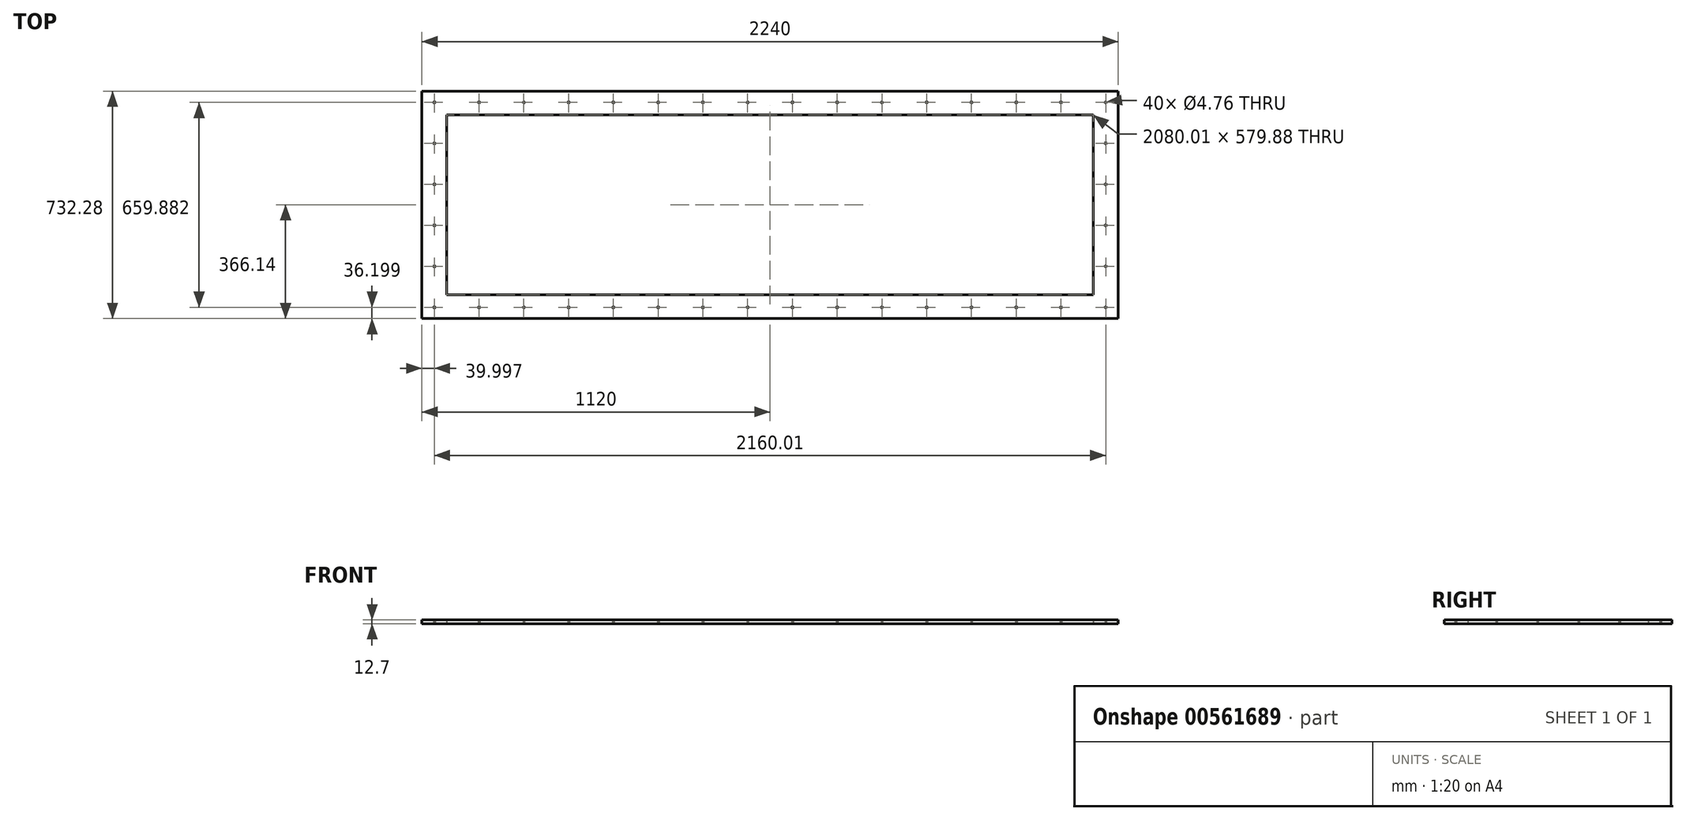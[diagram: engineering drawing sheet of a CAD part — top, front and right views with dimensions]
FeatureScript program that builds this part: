
annotation { "Feature Type Name" : "Feature", "Feature Type Description" : "" }
export const myFeature = defineFeature(function(context is Context, id is Id, definition is map)
    precondition{}
    {
        {
            var Q0;
            Q0=qCreatedBy(makeId("Top.planeOp"),FACE);
            var sketch = newSketch(context, id + "F0", { "sketchPlane" : qUnion([Q0])});
            skLineSegment(sketch, "E0.bottom", {"start": v(1040, 289.94) * mm, "end": v(-1040, 289.94) * mm});
            skLineSegment(sketch, "E0.top", {"start": v(1040, -289.94) * mm, "end": v(-1040, -289.94) * mm});
            skLineSegment(sketch, "E0.left", {"start": v(1040, 289.94) * mm, "end": v(1040, -289.94) * mm});
            skLineSegment(sketch, "E0.right", {"start": v(-1040, 289.94) * mm, "end": v(-1040, -289.94) * mm});
            skPoint(sketch, "E0.middle", {"position": v(0, 0) * mm});
            skLineSegment(sketch, "E1.bottom", {"start": v(1120, 366.14) * mm, "end": v(-1120, 366.14) * mm});
            skLineSegment(sketch, "E1.top", {"start": v(1120, -366.14) * mm, "end": v(-1120, -366.14) * mm});
            skLineSegment(sketch, "E1.left", {"start": v(1120, 366.14) * mm, "end": v(1120, -366.14) * mm});
            skLineSegment(sketch, "E1.right", {"start": v(-1120, 366.14) * mm, "end": v(-1120, -366.14) * mm});
            skLineSegment(sketch, "E2.bottom", {"start": v(1080, 329.94) * mm, "end": v(-1080, 329.94) * mm, "construction": true});
            skLineSegment(sketch, "E2.top", {"start": v(1080, -329.94) * mm, "end": v(-1080, -329.94) * mm, "construction": true});
            skLineSegment(sketch, "E2.left", {"start": v(1080, 329.94) * mm, "end": v(1080, -329.94) * mm, "construction": true});
            skLineSegment(sketch, "E2.right", {"start": v(-1080, 329.94) * mm, "end": v(-1080, -329.94) * mm, "construction": true});
            skPoint(sketch, "E3", {"position": v(-1080, 329.94) * mm});
            skPoint(sketch, "E4", {"position": v(1080, 329.94) * mm});
            skPoint(sketch, "E5", {"position": v(1080, -329.94) * mm});
            skPoint(sketch, "E6", {"position": v(-1080, -329.94) * mm});
            skPoint(sketch, "E7.1.0.0", {"position": v(-936, 329.94) * mm});
            skPoint(sketch, "E7.2.0.0", {"position": v(-792, 329.94) * mm});
            skPoint(sketch, "E7.3.0.0", {"position": v(-648, 329.94) * mm});
            skPoint(sketch, "E7.4.0.0", {"position": v(-504, 329.94) * mm});
            skPoint(sketch, "E7.5.0.0", {"position": v(-360, 329.94) * mm});
            skPoint(sketch, "E7.6.0.0", {"position": v(-216, 329.94) * mm});
            skPoint(sketch, "E7.7.0.0", {"position": v(-72, 329.94) * mm});
            skPoint(sketch, "E7.8.0.0", {"position": v(72, 329.94) * mm});
            skPoint(sketch, "E7.9.0.0", {"position": v(216, 329.94) * mm});
            skPoint(sketch, "E7.10.0.0", {"position": v(360, 329.94) * mm});
            skPoint(sketch, "E7.11.0.0", {"position": v(504, 329.94) * mm});
            skPoint(sketch, "E7.12.0.0", {"position": v(648, 329.94) * mm});
            skPoint(sketch, "E7.13.0.0", {"position": v(792, 329.94) * mm});
            skPoint(sketch, "E7.14.0.0", {"position": v(936, 329.94) * mm});
            skLineSegment(sketch, "E7.direction1", {"start": v(-1080, 329.94) * mm, "end": v(-936, 329.94) * mm, "construction": true});
            skPoint(sketch, "E8.0.1.0", {"position": v(-1080, 197.96) * mm});
            skPoint(sketch, "E8.0.2.0", {"position": v(-1080, 65.98) * mm});
            skPoint(sketch, "E8.0.3.0", {"position": v(-1080, -66) * mm});
            skPoint(sketch, "E8.0.4.0", {"position": v(-1080, -197.97) * mm});
            skPoint(sketch, "E8.0.5.0", {"position": v(-1080, -329.95) * mm});
            skLineSegment(sketch, "E8.direction1", {"start": v(-1080, 329.94) * mm, "end": v(-1054.6, 329.94) * mm, "construction": true});
            skLineSegment(sketch, "E8.direction2", {"start": v(-1080, 329.94) * mm, "end": v(-1080, 197.96) * mm, "construction": true});
            skPoint(sketch, "E9.1.0.0", {"position": v(-936, -329.94) * mm});
            skPoint(sketch, "E9.2.0.0", {"position": v(-792, -329.94) * mm});
            skPoint(sketch, "E9.3.0.0", {"position": v(-648, -329.94) * mm});
            skPoint(sketch, "E9.4.0.0", {"position": v(-504, -329.94) * mm});
            skPoint(sketch, "E9.5.0.0", {"position": v(-360, -329.94) * mm});
            skPoint(sketch, "E9.6.0.0", {"position": v(-216, -329.94) * mm});
            skPoint(sketch, "E9.7.0.0", {"position": v(-72, -329.94) * mm});
            skPoint(sketch, "E9.8.0.0", {"position": v(72, -329.94) * mm});
            skPoint(sketch, "E9.9.0.0", {"position": v(216, -329.94) * mm});
            skPoint(sketch, "E9.10.0.0", {"position": v(360, -329.94) * mm});
            skPoint(sketch, "E9.11.0.0", {"position": v(504, -329.94) * mm});
            skPoint(sketch, "E9.12.0.0", {"position": v(648, -329.94) * mm});
            skPoint(sketch, "E9.13.0.0", {"position": v(792, -329.94) * mm});
            skPoint(sketch, "E9.14.0.0", {"position": v(936, -329.94) * mm});
            skLineSegment(sketch, "E9.direction1", {"start": v(-1080, -329.94) * mm, "end": v(-936, -329.94) * mm, "construction": true});
            skPoint(sketch, "E10.0.1.0", {"position": v(1080, -197.96) * mm});
            skPoint(sketch, "E10.0.2.0", {"position": v(1080, -65.98) * mm});
            skPoint(sketch, "E10.0.3.0", {"position": v(1080, 66) * mm});
            skPoint(sketch, "E10.0.4.0", {"position": v(1080, 197.97) * mm});
            skPoint(sketch, "E10.0.5.0", {"position": v(1080, 329.95) * mm});
            skLineSegment(sketch, "E10.direction1", {"start": v(1080, -329.94) * mm, "end": v(1080, -329.94) * mm});
            skLineSegment(sketch, "E10.direction2", {"start": v(1080, -329.94) * mm, "end": v(1080, -197.96) * mm, "construction": true});
            skSolve(sketch);
        }
        {
            var Q0;
            Q0=makeQuery(id+"F0.imprint","IMPRINT",FACE,{"disambiguationData":[TD([[makeQuery(id+"F0.imprint","IMPRINT",EDGE,{"derivedFrom":sQuery(id+"F0.wireOp",EDGE,"E0.bottom")}),-1.0]])]});
            extrude(context, id + "F1", {"entities" : qUnion([Q0]), "depth" : 12.7 * mm, "offsetDistance" : 25.4 * mm});
        }
        {
            var Q0;
            Q0=sQuery(id+"F0.wireOp",VERTEX,"E7.1.0.0");
            var Q1;
            Q1=sQuery(id+"F0.wireOp",VERTEX,"E7.2.0.0");
            var Q2;
            Q2=sQuery(id+"F0.wireOp",VERTEX,"E7.3.0.0");
            var Q3;
            Q3=sQuery(id+"F0.wireOp",VERTEX,"E7.4.0.0");
            var Q4;
            Q4=sQuery(id+"F0.wireOp",VERTEX,"E7.5.0.0");
            var Q5;
            Q5=sQuery(id+"F0.wireOp",VERTEX,"E2.right.start");
            var Q6;
            Q6=sQuery(id+"F0.wireOp",VERTEX,"E8.0.1.0");
            var Q7;
            Q7=sQuery(id+"F0.wireOp",VERTEX,"E8.0.2.0");
            var Q8;
            Q8=sQuery(id+"F0.wireOp",VERTEX,"E8.0.4.0");
            var Q9;
            Q9=sQuery(id+"F0.wireOp",VERTEX,"E2.right.end");
            var Q10;
            Q10=sQuery(id+"F0.wireOp",VERTEX,"E9.1.0.0");
            var Q11;
            Q11=sQuery(id+"F0.wireOp",VERTEX,"E9.2.0.0");
            var Q12;
            Q12=sQuery(id+"F0.wireOp",VERTEX,"E8.0.3.0");
            var Q13;
            Q13=sQuery(id+"F0.wireOp",VERTEX,"E9.3.0.0");
            var Q14;
            Q14=sQuery(id+"F0.wireOp",VERTEX,"E9.4.0.0");
            var Q15;
            Q15=sQuery(id+"F0.wireOp",VERTEX,"E9.5.0.0");
            var Q16;
            Q16=sQuery(id+"F0.wireOp",VERTEX,"E9.6.0.0");
            var Q17;
            Q17=sQuery(id+"F0.wireOp",VERTEX,"E9.7.0.0");
            var Q18;
            Q18=sQuery(id+"F0.wireOp",VERTEX,"E9.9.0.0");
            var Q19;
            Q19=sQuery(id+"F0.wireOp",VERTEX,"E9.8.0.0");
            var Q20;
            Q20=sQuery(id+"F0.wireOp",VERTEX,"E9.10.0.0");
            var Q21;
            Q21=sQuery(id+"F0.wireOp",VERTEX,"E9.11.0.0");
            var Q22;
            Q22=sQuery(id+"F0.wireOp",VERTEX,"E9.12.0.0");
            var Q23;
            Q23=sQuery(id+"F0.wireOp",VERTEX,"E9.13.0.0");
            var Q24;
            Q24=sQuery(id+"F0.wireOp",VERTEX,"E9.14.0.0");
            var Q25;
            Q25=sQuery(id+"F0.wireOp",VERTEX,"E5");
            var Q26;
            Q26=sQuery(id+"F0.wireOp",VERTEX,"E10.direction2.end");
            var Q27;
            Q27=sQuery(id+"F0.wireOp",VERTEX,"E10.0.2.0");
            var Q28;
            Q28=sQuery(id+"F0.wireOp",VERTEX,"E10.0.3.0");
            var Q29;
            Q29=sQuery(id+"F0.wireOp",VERTEX,"E10.0.4.0");
            var Q30;
            Q30=sQuery(id+"F0.wireOp",VERTEX,"E4");
            var Q31;
            Q31=sQuery(id+"F0.wireOp",VERTEX,"E7.14.0.0");
            var Q32;
            Q32=sQuery(id+"F0.wireOp",VERTEX,"E7.13.0.0");
            var Q33;
            Q33=sQuery(id+"F0.wireOp",VERTEX,"E7.12.0.0");
            var Q34;
            Q34=sQuery(id+"F0.wireOp",VERTEX,"E7.11.0.0");
            var Q35;
            Q35=sQuery(id+"F0.wireOp",VERTEX,"E7.10.0.0");
            var Q36;
            Q36=sQuery(id+"F0.wireOp",VERTEX,"E7.9.0.0");
            var Q37;
            Q37=sQuery(id+"F0.wireOp",VERTEX,"E7.8.0.0");
            var Q38;
            Q38=sQuery(id+"F0.wireOp",VERTEX,"E7.7.0.0");
            var Q39;
            Q39=sQuery(id+"F0.wireOp",VERTEX,"E7.6.0.0");
            var Q40;
            Q40=sQuery(id+"F0.wireOp",VERTEX,"E7.7.0.0");
            var Q41;
            Q41=makeQuery(id+"F1.opExtrude","SWEPT_BODY",BODY,{"disambiguationData":[OSD([sQuery(id+"F0.wireOp",EDGE,"E0.bottom"),sQuery(id+"F0.wireOp",EDGE,"E0.top"),sQuery(id+"F0.wireOp",EDGE,"E0.left"),sQuery(id+"F0.wireOp",EDGE,"E0.right"),sQuery(id+"F0.wireOp",EDGE,"E1.bottom"),sQuery(id+"F0.wireOp",EDGE,"E1.top"),sQuery(id+"F0.wireOp",EDGE,"E1.left"),sQuery(id+"F0.wireOp",EDGE,"E1.right")])]});
            hole(context, id + "F2", {"style" : HoleStyle.SIMPLE, "endStyle" : HoleEndStyle.THROUGH, "oppositeDirection" : true, "holeDiameter" : 4.76 * mm, "isTappedThrough" : true, "tappedDepth" : 12.7 * mm, "tapClearance" : 3, "locations" : qUnion([Q0, Q1, Q2, Q3, Q4, Q5, Q6, Q7, Q8, Q9, Q10, Q11, Q12, Q13, Q14, Q15, Q16, Q17, Q18, Q19, Q20, Q21, Q22, Q23, Q24, Q25, Q26, Q27, Q28, Q29, Q30, Q31, Q32, Q33, Q34, Q35, Q36, Q37, Q38, Q39, Q40]), "scope" : qUnion([Q41])});
        }
    });
